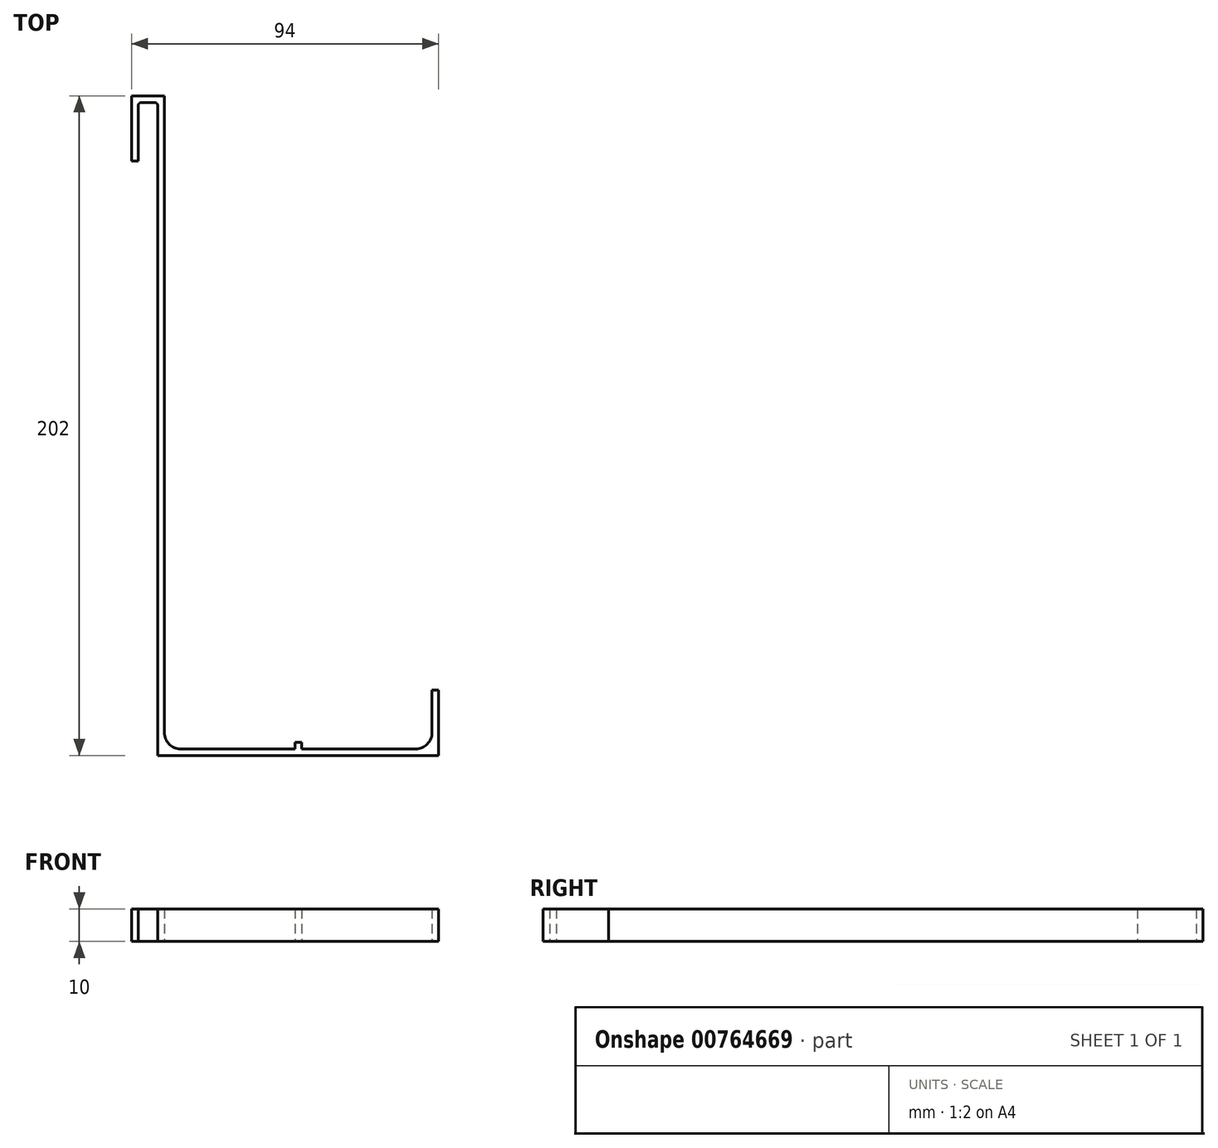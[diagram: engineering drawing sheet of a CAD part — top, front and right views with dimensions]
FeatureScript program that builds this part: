
annotation { "Feature Type Name" : "Feature", "Feature Type Description" : "" }
export const myFeature = defineFeature(function(context is Context, id is Id, definition is map)
    precondition{}
    {
        {
            var Q0;
            Q0=qCreatedBy(makeId("Top.planeOp"),FACE);
            var sketch = newSketch(context, id + "F0", { "sketchPlane" : qUnion([Q0])});
            skLineSegment(sketch, "E0", {"start": v(-6, 182) * mm, "end": v(-8, 182) * mm});
            skLineSegment(sketch, "E1", {"start": v(-8, 182) * mm, "end": v(-8, 202) * mm});
            skLineSegment(sketch, "E2", {"start": v(-8, 202) * mm, "end": v(2, 202) * mm});
            skLineSegment(sketch, "E3", {"start": v(2, 202) * mm, "end": v(2, 2) * mm});
            skLineSegment(sketch, "E4", {"start": v(2, 2) * mm, "end": v(42, 2) * mm});
            skLineSegment(sketch, "E5", {"start": v(42, 2) * mm, "end": v(42, 4) * mm});
            skLineSegment(sketch, "E6", {"start": v(42, 4) * mm, "end": v(44, 4) * mm});
            skLineSegment(sketch, "E7", {"start": v(44, 4) * mm, "end": v(44, 2) * mm});
            skLineSegment(sketch, "E8", {"start": v(44, 2) * mm, "end": v(84, 2) * mm});
            skLineSegment(sketch, "E9", {"start": v(84, 2) * mm, "end": v(84, 20) * mm});
            skLineSegment(sketch, "E10", {"start": v(84, 20) * mm, "end": v(86, 20) * mm});
            skLineSegment(sketch, "E11", {"start": v(86, 20) * mm, "end": v(86, 0) * mm});
            skLineSegment(sketch, "E12", {"start": v(86, 0) * mm, "end": v(0, 0) * mm});
            skLineSegment(sketch, "E13", {"start": v(0, 0) * mm, "end": v(0, 200) * mm});
            skLineSegment(sketch, "E14", {"start": v(0, 200) * mm, "end": v(-6, 200) * mm});
            skLineSegment(sketch, "E15", {"start": v(-6, 200) * mm, "end": v(-6, 182) * mm});
            skSolve(sketch);
        }
        {
            var Q0;
            Q0 = qSketchRegion(id + "F0", true);
            extrude(context, id + "F1", {"entities" : qUnion([Q0]), "depth" : 10 * mm, "offsetDistance" : 25 * mm});
        }
        {
            var Q0;
            Q0=makeQuery(id+"F1.opExtrude","SWEPT_EDGE",EDGE,{"disambiguationData":[OSD([sQuery(id+"F0.wireOp",EDGE,"E3"),sQuery(id+"F0.wireOp",EDGE,"E4")])]});
            var Q1;
            Q1=makeQuery(id+"F1.opExtrude","SWEPT_EDGE",EDGE,{"disambiguationData":[OSD([sQuery(id+"F0.wireOp",EDGE,"E8"),sQuery(id+"F0.wireOp",EDGE,"E9")])]});
            fillet(context, id + "F2", {"entities" : qUnion([Q0, Q1]), "radius" : 5 * mm, "tangentPropagation" : true, "allowEdgeOverflow" : false});
        }
        {
            var Q0;
            Q0=makeQuery(id+"F1.opExtrude","SWEPT_EDGE",EDGE,{"disambiguationData":[OSD([sQuery(id+"F0.wireOp",EDGE,"E14"),sQuery(id+"F0.wireOp",EDGE,"E15")])]});
            var Q1;
            Q1=makeQuery(id+"F1.opExtrude","SWEPT_EDGE",EDGE,{"disambiguationData":[OSD([sQuery(id+"F0.wireOp",EDGE,"E13"),sQuery(id+"F0.wireOp",EDGE,"E14")])]});
            fillet(context, id + "F3", {"entities" : qUnion([Q0, Q1]), "radius" : 1 * mm, "tangentPropagation" : true, "allowEdgeOverflow" : false});
        }
    });
